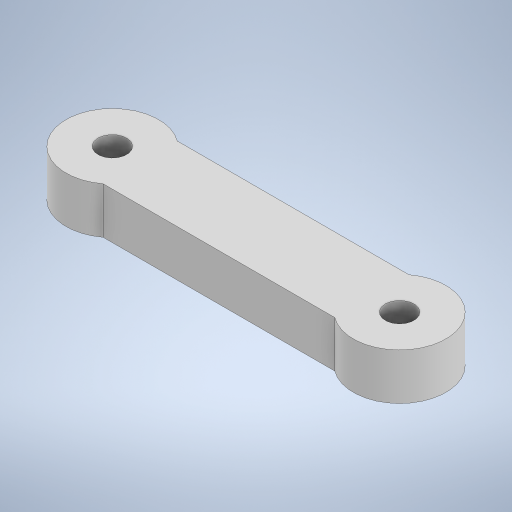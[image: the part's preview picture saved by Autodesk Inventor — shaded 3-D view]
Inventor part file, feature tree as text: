
AUTODESK INVENTOR PART (.ipt)
format: ipt  version: 2024.2 (Build 282272000, 272)  size: 257,024 bytes
history: native  units: in
note: dims shown in document units (in); Inventor stores cm internally (conversion verified against a paired STEP export)
features: sketch x2, extrude x1, hole x1, plane x1, projected_geometry x1
ambient origin geometry x8: Origin, YZ Plane, XZ Plane, XY Plane, X Axis, Y Axis, Z Axis, Center Point
bodies: Solid1 (feature_tree)
feature tree (6):
  extrude  "Extrusion1"  Depth=0.3937in
  hole  "Hole1"  [1 undecoded]
  plane  "Work Plane1"
  sketch  "Sketch1"  dims[d0=0.3937in d1=0.3937in]
  sketch  "Sketch2"  dims[d2=0.1575in d3=0.1575in d6=0.1969in d7=0.0in d8=0.122in d9=0.1575in d10=0.1575in d11=0.0787in d12=90.0deg d13=0.1575in d14=0.0in d18=-0.1378in d27=0.9843in]
  projected_geometry  "Projected Loop1"
note: 1 required parameter value undecoded (feature->parameter linkage not recoverable at this tier; creation-order binding heuristic only, values carry confidence <= 0.55)
